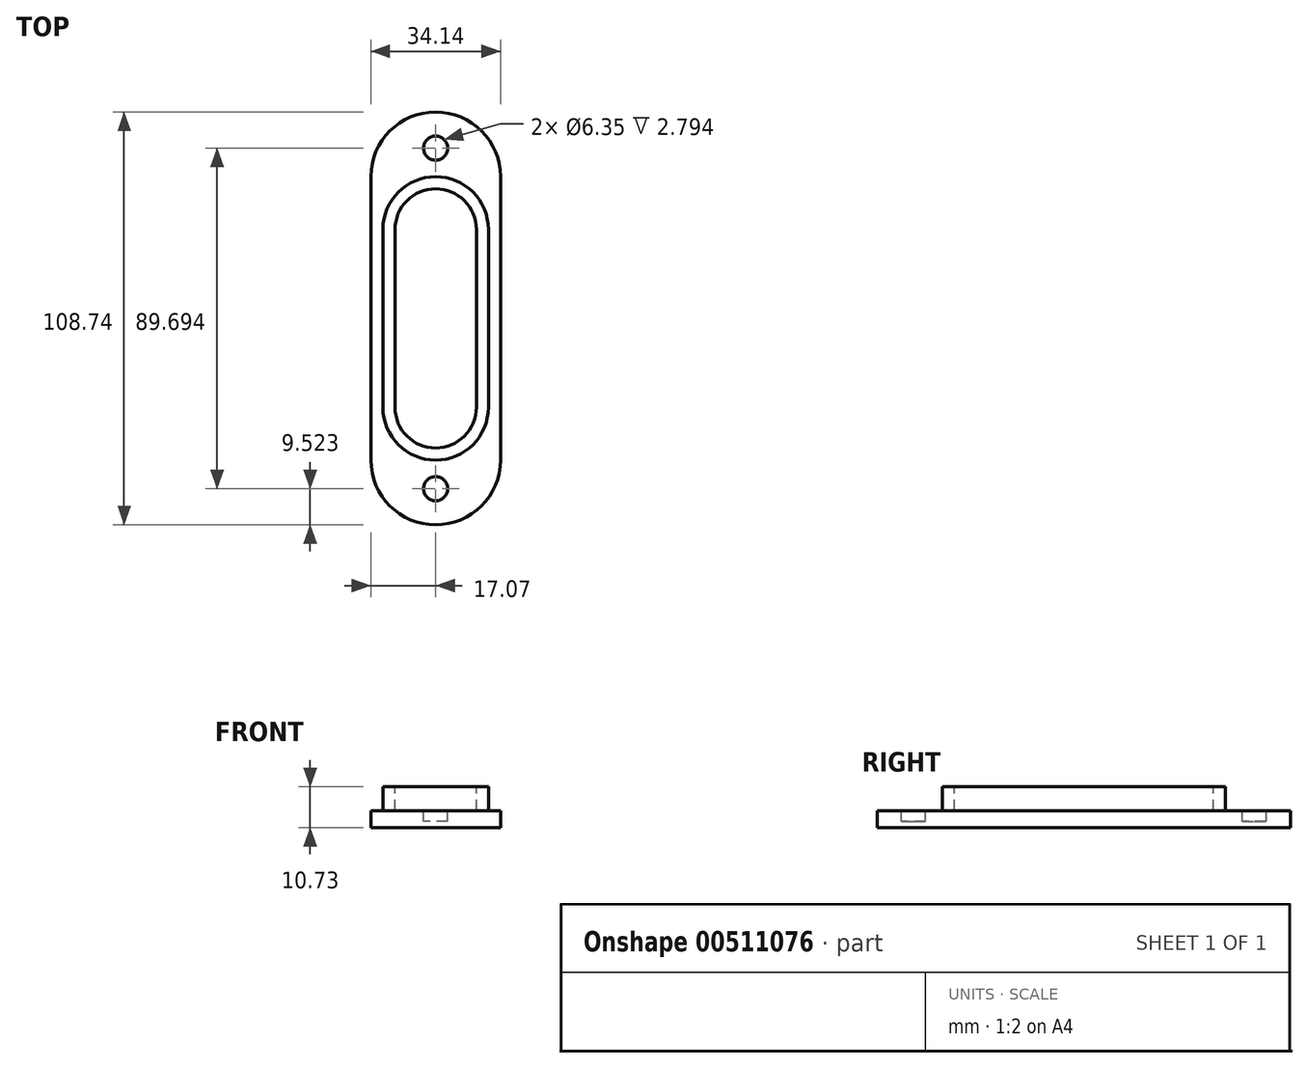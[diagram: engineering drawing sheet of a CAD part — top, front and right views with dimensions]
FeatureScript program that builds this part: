
annotation { "Feature Type Name" : "Feature", "Feature Type Description" : "" }
export const myFeature = defineFeature(function(context is Context, id is Id, definition is map)
    precondition{}
    {
        {
            var Q0;
            Q0=qCreatedBy(makeId("Top.planeOp"),FACE);
            var sketch = newSketch(context, id + "F0", { "sketchPlane" : qUnion([Q0])});
            skLineSegment(sketch, "E0.bottom", {"start": v(-13.9, 23.42) * mm, "end": v(13.9, 23.42) * mm, "construction": true});
            skLineSegment(sketch, "E0.top", {"start": v(-13.9, -23.42) * mm, "end": v(13.9, -23.42) * mm, "construction": true});
            skLineSegment(sketch, "E0.left", {"start": v(-13.9, 23.42) * mm, "end": v(-13.9, -23.42) * mm});
            skLineSegment(sketch, "E0.right", {"start": v(13.9, 23.42) * mm, "end": v(13.9, -23.42) * mm});
            skPoint(sketch, "E0.middle", {"position": v(0, 0) * mm});
            skArc(sketch, "E1", {"start": v(13.9, 23.42) * mm, "mid": v(0, 37.3) * mm, "end": v(-13.9, 23.42) * mm});
            skArc(sketch, "E2", {"start": v(-13.9, -23.42) * mm, "mid": v(0, -37.3) * mm, "end": v(13.9, -23.42) * mm});
            skLineSegment(sketch, "E3.bottom", {"start": v(-17.07, 37.3) * mm, "end": v(17.07, 37.3) * mm, "construction": true});
            skLineSegment(sketch, "E3.top", {"start": v(-17.07, -37.3) * mm, "end": v(17.07, -37.3) * mm, "construction": true});
            skLineSegment(sketch, "E3.left", {"start": v(-17.07, 37.3) * mm, "end": v(-17.07, -37.3) * mm});
            skLineSegment(sketch, "E3.right", {"start": v(17.07, 37.3) * mm, "end": v(17.07, -37.3) * mm});
            skArc(sketch, "E4", {"start": v(17.07, 37.3) * mm, "mid": v(0, 54.37) * mm, "end": v(-17.07, 37.3) * mm});
            skArc(sketch, "E5", {"start": v(-17.07, -37.3) * mm, "mid": v(0, -54.37) * mm, "end": v(17.07, -37.3) * mm});
            skCircle(sketch, "E6", {"center": v(0, 44.85) * mm, "radius": 3.18 * mm});
            skCircle(sketch, "E7", {"center": v(0, -44.85) * mm, "radius": 3.18 * mm});
            skSolve(sketch);
        }
        {
            var Q0;
            Q0=makeQuery(id+"F0.imprint","IMPRINT",FACE,{"disambiguationData":[TD([[makeQuery(id+"F0.imprint","IMPRINT",EDGE,{"derivedFrom":sQuery(id+"F0.wireOp",EDGE,"E0.left")}),1.0]])]});
            extrude(context, id + "F1", {"entities" : qUnion([Q0]), "depth" : 6.35 * mm});
        }
        {
            var Q0;
            Q0=makeQuery(id+"F0.imprint","IMPRINT",FACE,{"disambiguationData":[TD([[makeQuery(id+"F0.imprint","IMPRINT",EDGE,{"derivedFrom":sQuery(id+"F0.wireOp",EDGE,"E0.left")}),-1.0]])]});
            var Q1;
            Q1=makeQuery(id+"F0.imprint","IMPRINT",FACE,{"disambiguationData":[TD([[makeQuery(id+"F0.imprint","IMPRINT",EDGE,{"derivedFrom":sQuery(id+"F0.wireOp",EDGE,"E0.left")}),1.0]])]});
            extrude(context, id + "F2", {"entities" : qUnion([Q0, Q1]), "operationType" : NewBodyOperationType.ADD, "oppositeDirection" : true, "depth" : 2.8 * mm});
        }
        {
            var Q0;
            Q0=makeQuery(id+"F2.opExtrude","CAP_FACE",FACE,{"disambiguationData":[OSD([sQuery(id+"F0.wireOp",EDGE,"E0.left"),sQuery(id+"F0.wireOp",EDGE,"E0.right"),sQuery(id+"F0.wireOp",EDGE,"E1"),sQuery(id+"F0.wireOp",EDGE,"E2"),sQuery(id+"F0.wireOp",EDGE,"E3.left"),sQuery(id+"F0.wireOp",EDGE,"E3.right"),sQuery(id+"F0.wireOp",EDGE,"E4"),sQuery(id+"F0.wireOp",EDGE,"E5"),sQuery(id+"F0.wireOp",EDGE,"E6"),sQuery(id+"F0.wireOp",EDGE,"E7")])],"isStart":false});
            var sketch = newSketch(context, id + "F3", { "sketchPlane" : qUnion([Q0])});
            skArc(sketch, "E8.0", {"start": v(-17.07, 37.3) * mm, "mid": v(0, 54.37) * mm, "end": v(17.07, 37.3) * mm});
            skLineSegment(sketch, "E9.0", {"start": v(17.07, -37.3) * mm, "end": v(17.07, 37.3) * mm});
            skArc(sketch, "E10.0", {"start": v(17.07, -37.3) * mm, "mid": v(0, -54.37) * mm, "end": v(-17.07, -37.3) * mm});
            skLineSegment(sketch, "E11.0", {"start": v(-17.07, -37.3) * mm, "end": v(-17.07, 37.3) * mm});
            skSolve(sketch);
        }
        {
            var Q0;
            Q0 = qSketchRegion(id + "F3", true);
            extrude(context, id + "F4", {"entities" : qUnion([Q0]), "operationType" : NewBodyOperationType.ADD, "depth" : 1.59 * mm});
        }
        {
            var Q0;
            Q0=makeQuery(id+"F1.opExtrude","CAP_FACE",FACE,{"disambiguationData":[OSD([sQuery(id+"F0.wireOp",EDGE,"E0.left"),sQuery(id+"F0.wireOp",EDGE,"E0.right"),sQuery(id+"F0.wireOp",EDGE,"E1"),sQuery(id+"F0.wireOp",EDGE,"E2")])],"isStart":false});
            var sketch = newSketch(context, id + "F5", { "sketchPlane" : qUnion([Q0])});
            skLineSegment(sketch, "E12.0", {"start": v(-10.72, 23.42) * mm, "end": v(-10.72, -23.42) * mm});
            skArc(sketch, "E12.1", {"start": v(10.72, 23.42) * mm, "mid": v(0, 34.13) * mm, "end": v(-10.72, 23.42) * mm});
            skLineSegment(sketch, "E12.2", {"start": v(10.72, 23.42) * mm, "end": v(10.72, -23.42) * mm});
            skArc(sketch, "E12.3", {"start": v(-10.72, -23.42) * mm, "mid": v(0, -34.13) * mm, "end": v(10.72, -23.42) * mm});
            skSolve(sketch);
        }
        {
            var Q0;
            Q0=makeQuery(id+"F5.imprint","IMPRINT",FACE,{"disambiguationData":[TD([[makeQuery(id+"F5.imprint","IMPRINT",EDGE,{"derivedFrom":sQuery(id+"F5.wireOp",EDGE,"E12.0")}),1.0]])]});
            var Q1;
            Q1=makeQuery(id+"F2.opExtrude","CAP_FACE",FACE,{"disambiguationData":[OSD([sQuery(id+"F0.wireOp",EDGE,"E3.left"),sQuery(id+"F0.wireOp",EDGE,"E3.right"),sQuery(id+"F0.wireOp",EDGE,"E4"),sQuery(id+"F0.wireOp",EDGE,"E5"),sQuery(id+"F0.wireOp",EDGE,"E6"),sQuery(id+"F0.wireOp",EDGE,"E7")])],"isStart":true});
            extrude(context, id + "F6", {"entities" : qUnion([Q0]), "operationType" : NewBodyOperationType.REMOVE, "endBound" : BoundingType.UP_TO_SURFACE, "oppositeDirection" : true, "endBoundEntityFace" : qUnion([Q1]), "depth" : 6.35 * mm});
        }
    });
